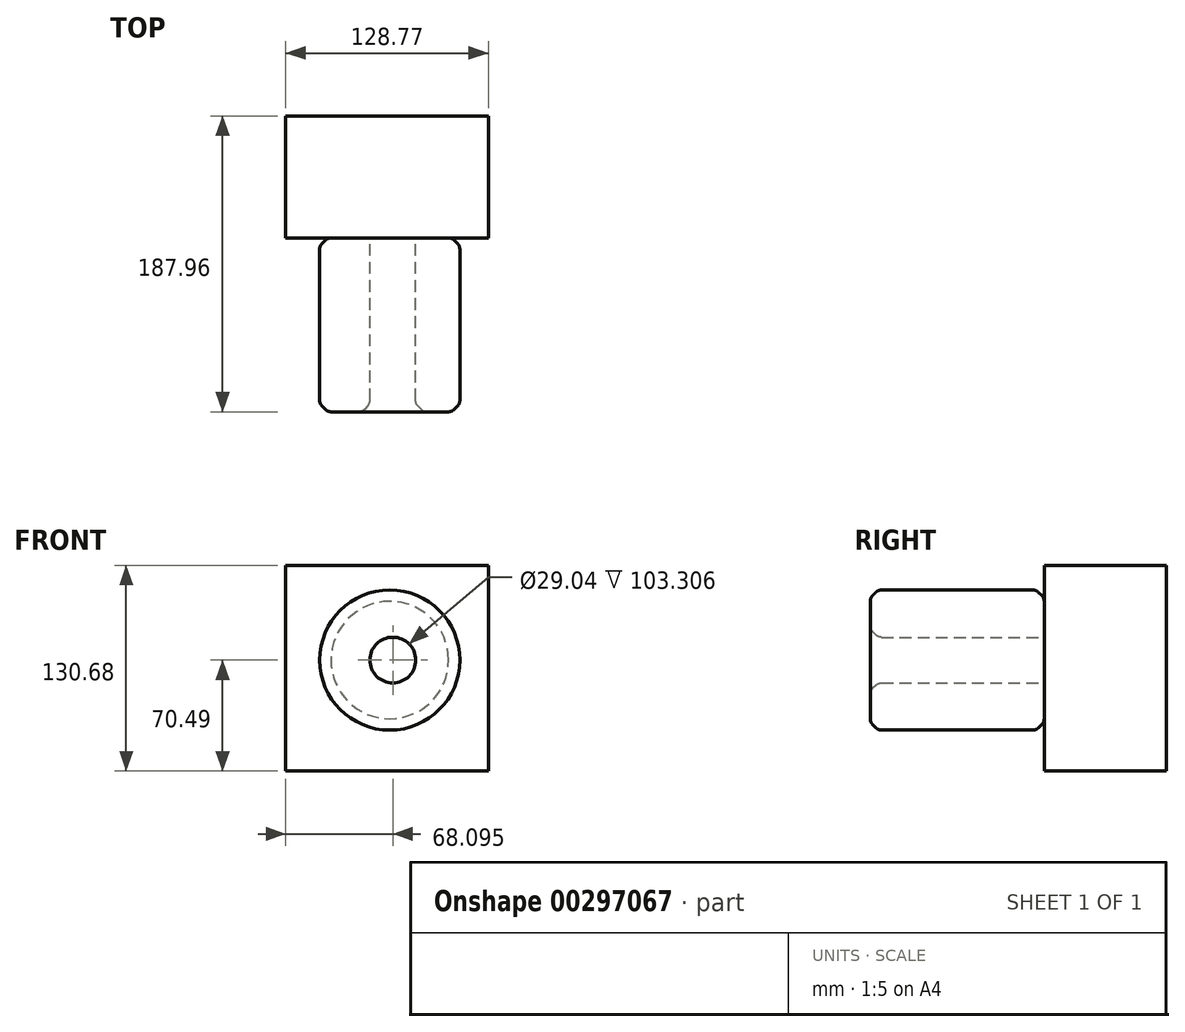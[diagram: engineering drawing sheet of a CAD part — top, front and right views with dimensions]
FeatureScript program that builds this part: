
annotation { "Feature Type Name" : "Feature", "Feature Type Description" : "" }
export const myFeature = defineFeature(function(context is Context, id is Id, definition is map)
    precondition{}
    {
        {
            var Q0;
            Q0=qCreatedBy(makeId("Front.planeOp"),FACE);
            var sketch = newSketch(context, id + "F0", { "sketchPlane" : qUnion([Q0])});
            skCircle(sketch, "E0", {"center": v(0, 0) * mm, "radius": 44.5 * mm});
            skSolve(sketch);
        }
        {
            var Q0;
            Q0=makeQuery(id+"F0.imprint","IMPRINT",FACE,{"disambiguationData":[TD([[makeQuery(id+"F0.imprint","IMPRINT",EDGE,{"derivedFrom":sQuery(id+"F0.wireOp",EDGE,"E0")}),1.0]])]});
            extrude(context, id + "F1", {"entities" : qUnion([Q0]), "depth" : 110.49 * mm});
        }
        {
            var Q0;
            Q0=qCreatedBy(makeId("Front.planeOp"),FACE);
            var sketch = newSketch(context, id + "F2", { "sketchPlane" : qUnion([Q0])});
            skCircle(sketch, "E1", {"center": v(1.97, 0) * mm, "radius": 14.52 * mm});
            skSolve(sketch);
        }
        {
            var Q0;
            Q0 = qSketchRegion(id + "F2", true);
            extrude(context, id + "F3", {"entities" : qUnion([Q0]), "operationType" : NewBodyOperationType.REMOVE, "depth" : 202.95 * mm});
        }
        {
            var Q0;
            Q0=makeQuery(id+"F3.boolean.opBoolean","INTERSECT",EDGE,{"derivedFrom":[makeQuery(id+"F1.opExtrude","CAP_FACE",FACE,{"disambiguationData":[OSD([sQuery(id+"F0.wireOp",EDGE,"E0")])],"isStart":false}),makeQuery(id+"F3.opExtrude","SWEPT_FACE",FACE,{"disambiguationData":[OSD([sQuery(id+"F2.wireOp",EDGE,"E1")])]})]});
            var Q1;
            Q1=makeQuery(id+"F3.boolean.opBoolean","COPY",EDGE,{"derivedFrom":makeQuery(id+"F3.opExtrude","CAP_EDGE",EDGE,{"disambiguationData":[OSD([sQuery(id+"F2.wireOp",EDGE,"E1")])],"isStart":true})});
            var Q2;
            Q2=makeQuery(id+"F1.opExtrude","CAP_EDGE",EDGE,{"disambiguationData":[OSD([sQuery(id+"F0.wireOp",EDGE,"E0")])],"isStart":false});
            var Q3;
            Q3=makeQuery(id+"F1.opExtrude","CAP_EDGE",EDGE,{"disambiguationData":[OSD([sQuery(id+"F0.wireOp",EDGE,"E0")])],"isStart":true});
            chamfer(context, id + "F4", {"entities" : qUnion([Q0, Q1, Q2, Q3]), "width" : 5.08 * mm, "tangentPropagation" : true});
        }
        {
            var Q0;
            {var subQ0=sQuery(id+"F0.wireOp",EDGE,"E0");Q0=makeQuery(id+"F4.opChamfer","BLEND_EDGE",EDGE,{"blendedFrom":[makeQuery(id+"F1.opExtrude","CAP_EDGE",EDGE,{"disambiguationData":[OSD([subQ0])],"isStart":false}),makeQuery(id+"F1.opExtrude","SWEPT_FACE",FACE,{"disambiguationData":[OSD([subQ0])]})],"blendedInto":[makeQuery(id+"F1.opExtrude","SWEPT_FACE",FACE,{"disambiguationData":[OSD([subQ0])]})]});}
            var Q1;
            {var subQ0=sQuery(id+"F0.wireOp",EDGE,"E0");Q1=makeQuery(id+"F4.opChamfer","BLEND_EDGE",EDGE,{"blendedFrom":[makeQuery(id+"F1.opExtrude","CAP_EDGE",EDGE,{"disambiguationData":[OSD([subQ0])],"isStart":false}),makeQuery(id+"F1.opExtrude","CAP_FACE",FACE,{"disambiguationData":[OSD([subQ0])],"isStart":false})],"blendedInto":[makeQuery(id+"F1.opExtrude","CAP_FACE",FACE,{"disambiguationData":[OSD([subQ0])],"isStart":false})]});}
            var Q2;
            {var subQ0=sQuery(id+"F0.wireOp",EDGE,"E0");Q2=makeQuery(id+"F4.opChamfer","BLEND_EDGE",EDGE,{"blendedFrom":[makeQuery(id+"F1.opExtrude","CAP_EDGE",EDGE,{"disambiguationData":[OSD([subQ0])],"isStart":true}),makeQuery(id+"F1.opExtrude","SWEPT_FACE",FACE,{"disambiguationData":[OSD([subQ0])]})],"blendedInto":[makeQuery(id+"F1.opExtrude","SWEPT_FACE",FACE,{"disambiguationData":[OSD([subQ0])]})]});}
            var Q3;
            {var subQ0=sQuery(id+"F0.wireOp",EDGE,"E0");Q3=makeQuery(id+"F4.opChamfer","BLEND_EDGE",EDGE,{"blendedFrom":[makeQuery(id+"F1.opExtrude","CAP_EDGE",EDGE,{"disambiguationData":[OSD([subQ0])],"isStart":true}),makeQuery(id+"F1.opExtrude","CAP_FACE",FACE,{"disambiguationData":[OSD([subQ0])],"isStart":true})],"blendedInto":[makeQuery(id+"F1.opExtrude","CAP_FACE",FACE,{"disambiguationData":[OSD([subQ0])],"isStart":true})]});}
            var Q4;
            {var subQ0=makeQuery(id+"F3.opExtrude","SWEPT_FACE",FACE,{"disambiguationData":[OSD([sQuery(id+"F2.wireOp",EDGE,"E1")])]});Q4=makeQuery(id+"F4.opChamfer","BLEND_EDGE",EDGE,{"blendedFrom":[makeQuery(id+"F3.boolean.opBoolean","INTERSECT",EDGE,{"derivedFrom":[makeQuery(id+"F1.opExtrude","CAP_FACE",FACE,{"disambiguationData":[OSD([sQuery(id+"F0.wireOp",EDGE,"E0")])],"isStart":false}),subQ0]}),makeQuery(id+"F3.boolean.opBoolean","COPY",FACE,{"derivedFrom":subQ0})],"blendedInto":[makeQuery(id+"F3.boolean.opBoolean","COPY",FACE,{"derivedFrom":subQ0})]});}
            var Q5;
            {var subQ0=makeQuery(id+"F1.opExtrude","CAP_FACE",FACE,{"disambiguationData":[OSD([sQuery(id+"F0.wireOp",EDGE,"E0")])],"isStart":false});Q5=makeQuery(id+"F4.opChamfer","BLEND_EDGE",EDGE,{"blendedFrom":[makeQuery(id+"F3.boolean.opBoolean","INTERSECT",EDGE,{"derivedFrom":[subQ0,makeQuery(id+"F3.opExtrude","SWEPT_FACE",FACE,{"disambiguationData":[OSD([sQuery(id+"F2.wireOp",EDGE,"E1")])]})]}),subQ0],"blendedInto":[subQ0]});}
            var Q6;
            Q6=makeQuery(id+"F4.opChamfer","BLEND_FACE",FACE,{"disambiguationData":[OSD([sQuery(id+"F2.wireOp",EDGE,"E1")])]});
            fillet(context, id + "F5", {"entities" : qUnion([Q0, Q1, Q2, Q3, Q4, Q5, Q6]), "radius" : 5.08 * mm, "tangentPropagation" : true, "allowEdgeOverflow" : false});
        }
        {
            var Q0;
            Q0=qCreatedBy(makeId("Front.planeOp"),FACE);
            var sketch = newSketch(context, id + "F6", { "sketchPlane" : qUnion([Q0])});
            skLineSegment(sketch, "E2.bottom", {"start": v(62.64, 60.19) * mm, "end": v(-66.13, 60.19) * mm});
            skLineSegment(sketch, "E2.top", {"start": v(62.64, -70.5) * mm, "end": v(-66.13, -70.5) * mm});
            skLineSegment(sketch, "E2.left", {"start": v(62.64, 60.19) * mm, "end": v(62.64, -70.5) * mm});
            skLineSegment(sketch, "E2.right", {"start": v(-66.13, 60.19) * mm, "end": v(-66.13, -70.5) * mm});
            skSolve(sketch);
        }
        {
            var Q0;
            Q0=makeQuery(id+"F6.imprint","IMPRINT",FACE,{"disambiguationData":[TD([[makeQuery(id+"F6.imprint","IMPRINT",EDGE,{"derivedFrom":sQuery(id+"F6.wireOp",EDGE,"E2.bottom")}),1.0]])]});
            extrude(context, id + "F7", {"entities" : qUnion([Q0]), "operationType" : NewBodyOperationType.ADD, "oppositeDirection" : true, "depth" : 77.47 * mm});
        }
    });
